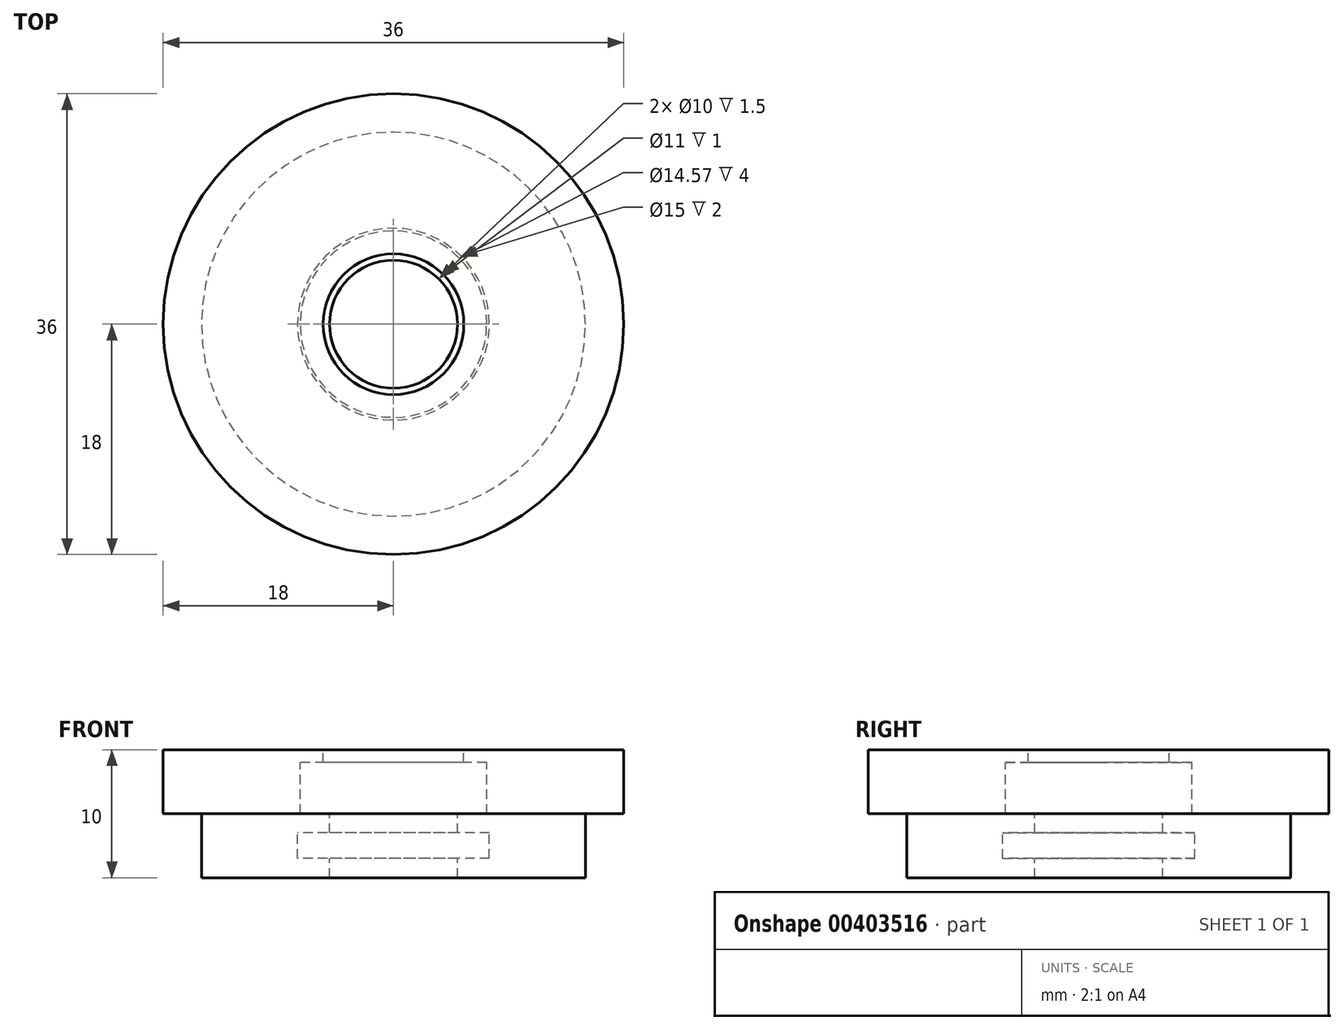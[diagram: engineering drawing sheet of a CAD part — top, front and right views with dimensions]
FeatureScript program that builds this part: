
annotation { "Feature Type Name" : "Feature", "Feature Type Description" : "" }
export const myFeature = defineFeature(function(context is Context, id is Id, definition is map)
    precondition{}
    {
        {
            var Q0;
            Q0=qCreatedBy(makeId("Top.planeOp"),FACE);
            var sketch = newSketch(context, id + "F0", { "sketchPlane" : qUnion([Q0])});
            skCircle(sketch, "E0", {"center": v(0, 0) * mm, "radius": 18 * mm});
            skSolve(sketch);
        }
        {
            var Q0;
            Q0=makeQuery(id+"F0.imprint","IMPRINT",FACE,{"disambiguationData":[TD([[makeQuery(id+"F0.imprint","IMPRINT",EDGE,{"derivedFrom":sQuery(id+"F0.wireOp",EDGE,"E0")}),1.0]])]});
            extrude(context, id + "F1", {"entities" : qUnion([Q0]), "depth" : 5 * mm});
        }
        {
            var Q0;
            Q0=makeQuery(id+"F1.opExtrude","CAP_FACE",FACE,{"disambiguationData":[OSD([sQuery(id+"F0.wireOp",EDGE,"E0")])],"isStart":true});
            var sketch = newSketch(context, id + "F2", { "sketchPlane" : qUnion([Q0])});
            skCircle(sketch, "E1", {"center": v(0, 0) * mm, "radius": 15 * mm});
            skSolve(sketch);
        }
        {
            var Q0;
            Q0=makeQuery(id+"F2.imprint","IMPRINT",FACE,{"disambiguationData":[TD([[makeQuery(id+"F2.imprint","IMPRINT",EDGE,{"derivedFrom":sQuery(id+"F2.wireOp",EDGE,"E1")}),1.0]])]});
            extrude(context, id + "F3", {"entities" : qUnion([Q0]), "operationType" : NewBodyOperationType.ADD, "depth" : 5 * mm});
        }
        {
            var Q0;
            Q0=makeQuery(id+"F1.opExtrude","CAP_FACE",FACE,{"disambiguationData":[OSD([sQuery(id+"F0.wireOp",EDGE,"E0")])],"isStart":false});
            var sketch = newSketch(context, id + "F4", { "sketchPlane" : qUnion([Q0])});
            skCircle(sketch, "E2", {"center": v(0, 0) * mm, "radius": 5 * mm});
            skSolve(sketch);
        }
        {
            var Q0;
            Q0=makeQuery(id+"F4.imprint","IMPRINT",FACE,{"disambiguationData":[TD([[makeQuery(id+"F4.imprint","IMPRINT",EDGE,{"derivedFrom":sQuery(id+"F4.wireOp",EDGE,"E2")}),1.0]])]});
            extrude(context, id + "F5", {"entities" : qUnion([Q0]), "operationType" : NewBodyOperationType.REMOVE, "oppositeDirection" : true, "depth" : 10 * mm});
        }
        {
            var Q0;
            Q0=makeQuery(id+"F1.opExtrude","CAP_FACE",FACE,{"disambiguationData":[OSD([sQuery(id+"F0.wireOp",EDGE,"E0")])],"isStart":false});
            var sketch = newSketch(context, id + "F6", { "sketchPlane" : qUnion([Q0])});
            skPoint(sketch, "E3.0", {"position": v(0, 0) * mm});
            skCircle(sketch, "E4", {"center": v(0, 0) * mm, "radius": 5.5 * mm});
            skSolve(sketch);
        }
        {
            var Q0;
            Q0 = qSketchRegion(id + "F6", true);
            extrude(context, id + "F7", {"entities" : qUnion([Q0]), "operationType" : NewBodyOperationType.REMOVE, "oppositeDirection" : true, "depth" : 5 * mm});
        }
        {
            var Q0;
            Q0=qCreatedBy(makeId("Right.planeOp"),FACE);
            var sketch = newSketch(context, id + "F8", { "sketchPlane" : qUnion([Q0])});
            skLineSegment(sketch, "E5", {"start": v(5.5, 5) * mm, "end": v(5.5, 0) * mm, "construction": true});
            skLineSegment(sketch, "E6", {"start": v(-5.5, 0) * mm, "end": v(-5.5, 0) * mm});
            skLineSegment(sketch, "E7", {"start": v(-18, 0) * mm, "end": v(-18, 5) * mm, "construction": true});
            skLineSegment(sketch, "E8", {"start": v(18, 5) * mm, "end": v(18, 0) * mm, "construction": true});
            skLineSegment(sketch, "E9.0.0", {"start": v(-18, 5) * mm, "end": v(18, 5) * mm, "construction": true});
            skLineSegment(sketch, "E10.0.0", {"start": v(18, 0) * mm, "end": v(-18, 0) * mm, "construction": true});
            skLineSegment(sketch, "E11.0.0", {"start": v(15, -5) * mm, "end": v(-15, -5) * mm, "construction": true});
            skPoint(sketch, "E12.oppositeSnap0", {"position": v(-5.5, 0) * mm});
            skLineSegment(sketch, "E12.bottom", {"start": v(-5.5, 4) * mm, "end": v(-7.29, 4) * mm});
            skLineSegment(sketch, "E12.top", {"start": v(-5.5, 0) * mm, "end": v(-7.29, 0) * mm});
            skLineSegment(sketch, "E12.left", {"start": v(-5.5, 4) * mm, "end": v(-5.5, 0) * mm});
            skLineSegment(sketch, "E12.right", {"start": v(-7.29, 4) * mm, "end": v(-7.29, 0) * mm});
            skSolve(sketch);
        }
        {
            var Q0;
            Q0=qCreatedBy(makeId("Right.planeOp"),FACE);
            var sketch = newSketch(context, id + "F9", { "sketchPlane" : qUnion([Q0])});
            skLineSegment(sketch, "E13", {"start": v(0, 0) * mm, "end": v(0, 4.95) * mm, "construction": true});
            skSolve(sketch);
        }
        {
            var Q0;
            Q0 = qSketchRegion(id + "F8", true);
            var Q1;
            Q1=sQuery(id+"F9.wireOp",EDGE,"E13");
            revolve(context, id + "F10", {"operationType" : NewBodyOperationType.REMOVE, "entities" : qUnion([Q0]), "axis" : qUnion([Q1]), "revolveType" : RevolveType.FULL, "oppositeDirection" : true});
        }
        {
            var Q0;
            Q0=qCreatedBy(makeId("Right.planeOp"),FACE);
            var sketch = newSketch(context, id + "F11", { "sketchPlane" : qUnion([Q0])});
            skLineSegment(sketch, "E14.bottom", {"start": v(7.5, -3.5) * mm, "end": v(5, -3.5) * mm});
            skLineSegment(sketch, "E14.top", {"start": v(7.5, -1.5) * mm, "end": v(5, -1.5) * mm});
            skLineSegment(sketch, "E14.left", {"start": v(7.5, -3.5) * mm, "end": v(7.5, -1.5) * mm});
            skLineSegment(sketch, "E14.right", {"start": v(5, -3.5) * mm, "end": v(5, -1.5) * mm});
            skLineSegment(sketch, "E15", {"start": v(15, 0) * mm, "end": v(15, -5) * mm, "construction": true});
            skLineSegment(sketch, "E16", {"start": v(-15, -5) * mm, "end": v(-15, 0) * mm, "construction": true});
            skLineSegment(sketch, "E17", {"start": v(5, 0) * mm, "end": v(5, -5) * mm, "construction": true});
            skLineSegment(sketch, "E18", {"start": v(-5, -5) * mm, "end": v(-5, 0) * mm, "construction": true});
            skLineSegment(sketch, "E19.0.0", {"start": v(18, 0) * mm, "end": v(-18, 0) * mm, "construction": true});
            skSolve(sketch);
        }
        {
            var Q0;
            Q0 = qSketchRegion(id + "F11", true);
            var Q1;
            Q1=sQuery(id+"F9.wireOp",EDGE,"E13");
            revolve(context, id + "F12", {"operationType" : NewBodyOperationType.REMOVE, "entities" : qUnion([Q0]), "axis" : qUnion([Q1]), "revolveType" : RevolveType.FULL, "oppositeDirection" : true});
        }
    });
